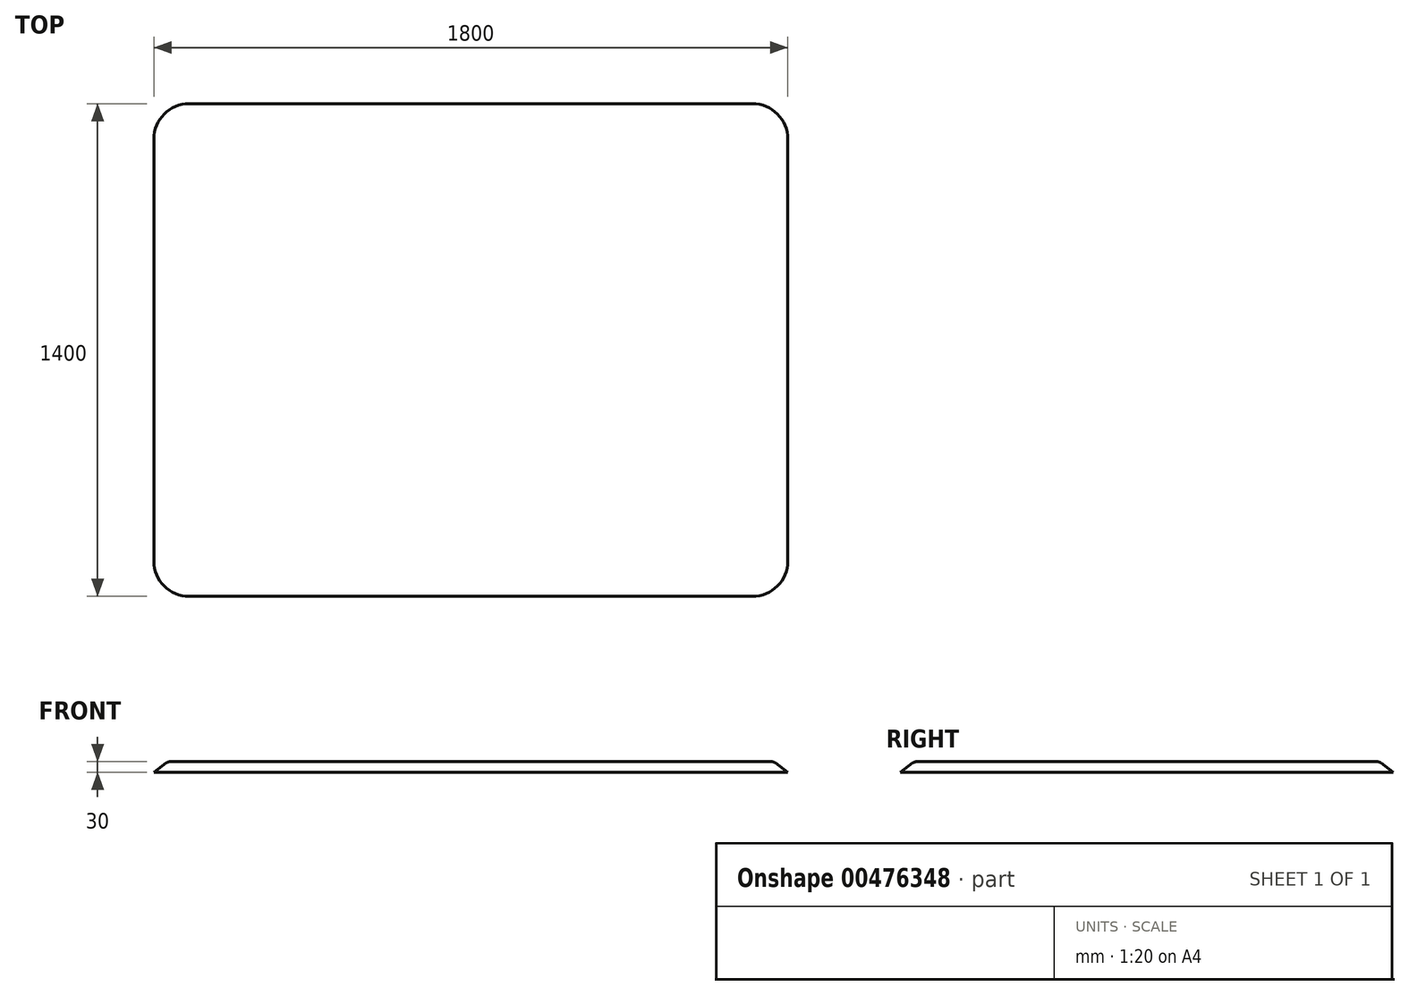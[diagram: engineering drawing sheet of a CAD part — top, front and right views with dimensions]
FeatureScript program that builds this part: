
annotation { "Feature Type Name" : "Feature", "Feature Type Description" : "" }
export const myFeature = defineFeature(function(context is Context, id is Id, definition is map)
    precondition{}
    {
        {
            var Q0;
            Q0=qCreatedBy(makeId("Top.planeOp"),FACE);
            var sketch = newSketch(context, id + "F0", { "sketchPlane" : qUnion([Q0])});
            skLineSegment(sketch, "E0.bottom", {"start": v(850, 650) * mm, "end": v(-850, 650) * mm});
            skLineSegment(sketch, "E0.top", {"start": v(850, -650) * mm, "end": v(-850, -650) * mm});
            skLineSegment(sketch, "E0.left", {"start": v(850, 650) * mm, "end": v(850, -650) * mm});
            skLineSegment(sketch, "E0.right", {"start": v(-850, 650) * mm, "end": v(-850, -650) * mm});
            skPoint(sketch, "E0.middle", {"position": v(0, 0) * mm});
            skSolve(sketch);
        }
        {
            var Q0;
            Q0=qSketchRegion(id+"F0",true);
            extrude(context, id + "F1", {"entities" : qUnion([Q0]), "depth" : 30 * mm});
        }
        {
            var Q0;
            Q0=makeQuery(id+"F1.opExtrude","SWEPT_EDGE",EDGE,{"disambiguationData":[OSD([sQuery(id+"F0.wireOp",EDGE,"E0.top"),sQuery(id+"F0.wireOp",EDGE,"E0.right")])]});
            var Q1;
            Q1=makeQuery(id+"F1.opExtrude","SWEPT_EDGE",EDGE,{"disambiguationData":[OSD([sQuery(id+"F0.wireOp",EDGE,"E0.bottom"),sQuery(id+"F0.wireOp",EDGE,"E0.right")])]});
            var Q2;
            Q2=makeQuery(id+"F1.opExtrude","SWEPT_EDGE",EDGE,{"disambiguationData":[OSD([sQuery(id+"F0.wireOp",EDGE,"E0.top"),sQuery(id+"F0.wireOp",EDGE,"E0.left")])]});
            var Q3;
            Q3=makeQuery(id+"F1.opExtrude","SWEPT_EDGE",EDGE,{"disambiguationData":[OSD([sQuery(id+"F0.wireOp",EDGE,"E0.bottom"),sQuery(id+"F0.wireOp",EDGE,"E0.left")])]});
            fillet(context, id + "F2", {"entities" : qUnion([Q0, Q1, Q2, Q3]), "radius" : 50 * mm, "tangentPropagation" : true, "allowEdgeOverflow" : false});
        }
        {
            var Q0;
            Q0=makeQuery(id+"F1.opExtrude","SWEPT_FACE",FACE,{"disambiguationData":[OSD([sQuery(id+"F0.wireOp",EDGE,"E0.top")])]});
            cPlane(context, id + "F3", {"entities" : qUnion([Q0]), "cplaneType" : CPlaneType.OFFSET, "offset" : 50 * mm, "oppositeDirection" : true, "width" : 152.4 * mm, "height" : 152.4 * mm});
        }
        {
            var Q0;
            Q0=qCreatedBy(id+"F3.planeOp",FACE);
            var sketch = newSketch(context, id + "F4", { "sketchPlane" : qUnion([Q0])});
            skPoint(sketch, "E1.0", {"position": v(850, 30) * mm});
            skPoint(sketch, "E2.0", {"position": v(850, 0) * mm});
            skLineSegment(sketch, "E3.0", {"start": v(850, 30) * mm, "end": v(850, 0) * mm});
            skLineSegment(sketch, "E4.top", {"start": v(850, 0) * mm, "end": v(900, 0) * mm, "construction": true});
            skLineSegment(sketch, "E4.left", {"start": v(850, 30) * mm, "end": v(850, 0) * mm, "construction": true});
            skLineSegment(sketch, "E4.right", {"start": v(900, 30) * mm, "end": v(900, 0) * mm, "construction": true});
            skLineSegment(sketch, "E5", {"start": v(850, 30) * mm, "end": v(853.33, 30) * mm});
            skLineSegment(sketch, "E6", {"start": v(865.33, 26) * mm, "end": v(900, 0) * mm});
            skPoint(sketch, "E7.visualSharp", {"position": v(860, 30) * mm});
            skArc(sketch, "E7.filletArc", {"start": v(865.33, 26) * mm, "mid": v(859.66, 28.97) * mm, "end": v(853.33, 30) * mm});
            skLineSegment(sketch, "E8", {"start": v(900, 0) * mm, "end": v(850, 0) * mm});
            skSolve(sketch);
        }
        {
            var Q0;
            Q0=makeQuery(id+"F1.opExtrude","CAP_FACE",FACE,{"disambiguationData":[OSD([sQuery(id+"F0.wireOp",EDGE,"E0.bottom"),sQuery(id+"F0.wireOp",EDGE,"E0.top"),sQuery(id+"F0.wireOp",EDGE,"E0.left"),sQuery(id+"F0.wireOp",EDGE,"E0.right")])],"isStart":false});
            var sketch = newSketch(context, id + "F5", { "sketchPlane" : qUnion([Q0])});
            skLineSegment(sketch, "E9.0.0", {"start": v(800, 650) * mm, "end": v(-800, 650) * mm});
            skArc(sketch, "E9.0.1", {"start": v(-800, 650) * mm, "mid": v(-835.36, 635.36) * mm, "end": v(-850, 600) * mm});
            skLineSegment(sketch, "E9.0.2", {"start": v(-850, 600) * mm, "end": v(-850, -600) * mm});
            skArc(sketch, "E9.0.3", {"start": v(-850, -600) * mm, "mid": v(-835.36, -635.36) * mm, "end": v(-800, -650) * mm});
            skLineSegment(sketch, "E9.0.4", {"start": v(-800, -650) * mm, "end": v(800, -650) * mm});
            skArc(sketch, "E9.0.5", {"start": v(800, -650) * mm, "mid": v(835.36, -635.36) * mm, "end": v(850, -600) * mm});
            skLineSegment(sketch, "E9.0.6", {"start": v(850, -600) * mm, "end": v(850, 600) * mm});
            skArc(sketch, "E9.0.7", {"start": v(850, 600) * mm, "mid": v(835.36, 635.36) * mm, "end": v(800, 650) * mm});
            skSolve(sketch);
        }
        {
            var Q0;
            Q0=makeQuery(id+"F4.imprint","IMPRINT",FACE,{"disambiguationData":[TD([[makeQuery(id+"F4.imprint","IMPRINT",EDGE,{"derivedFrom":sQuery(id+"F4.wireOp",EDGE,"E5")}),-1.0]])]});
            var Q1;
            Q1=qConstructionFilter(qBodyType(qCreatedBy(id+"F5",EDGE),BodyType.WIRE),ConstructionObject.NO);
            sweep(context, id + "F6", {"operationType" : NewBodyOperationType.ADD, "profiles" : qUnion([Q0]), "path" : qUnion([Q1])});
        }
    });
